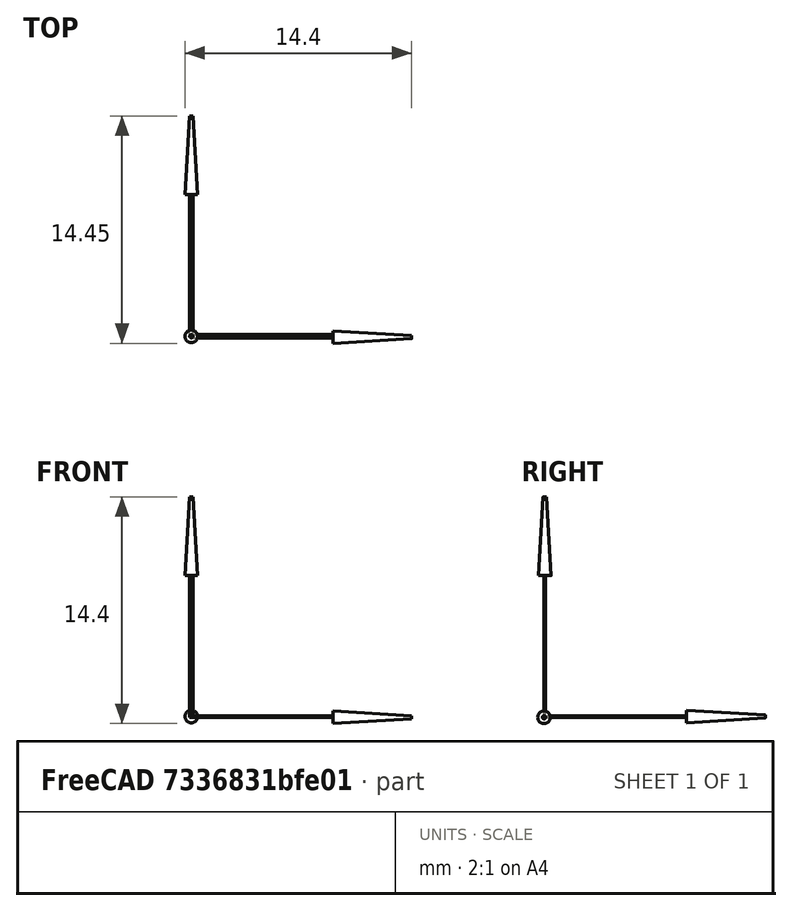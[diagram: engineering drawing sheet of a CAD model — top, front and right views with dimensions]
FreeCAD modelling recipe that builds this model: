
FCSTD DOCUMENT  (FreeCAD 0.16R6458 (Git))
Label: SSM-104-X-DH
License: All rights reserved
LicenseURL: http://en.wikipedia.org/wiki/All_rights_reserved
objects: Part::Feature×3, Sketcher::SketchObject×2, App::DocumentObjectGroup×1
note: 5 computed .brp shape members not serialized (recipe doc carries the construction recipe); baked Part::Feature solids carry a one-line shape summary decoded from their .brp

FEATURE [Part::Feature] FusionAxisZ1  label="Z"
  shape: bbox 0.8 x 0.8 x 14 mm, 8 faces (baked)
FEATURE [Part::Feature] FusionAxisY1  label="Y"
  Placement = pos=(0,0,0.05) rot=(-1,0,0;1.5708rad)
  shape: bbox 0.8 x 14 x 0.8 mm, 8 faces (baked)
FEATURE [Part::Feature] FusionAxisX1  label="X"
  Placement = pos=(0,-0.05,0) rot=(0,1,0;1.5708rad)
  shape: bbox 14 x 0.8 x 0.8 mm, 8 faces (baked)
FEATURE [App::DocumentObjectGroup] axis
  Group = -> [FusionAxisZ1,FusionAxisY1,FusionAxisX1]
FEATURE [Sketcher::SketchObject] Sketch  label="Footprint_Helper"
  expr: Constraints[124] = 4 * 2.54mm
  sketch-geometry (51):
    g0: LineSegment StartX=-11.98 StartY=4.32 StartZ=0 EndX=-9.695 EndY=4.32 EndZ=0
    g1: LineSegment StartX=-9.695 StartY=4.32 StartZ=0 EndX=-9.695 EndY=3.3 EndZ=0
    g2: LineSegment StartX=-9.695 StartY=3.3 StartZ=0 EndX=-11.98 EndY=3.3 EndZ=0
    g3: LineSegment StartX=-11.98 StartY=3.3 StartZ=0 EndX=-11.98 EndY=4.32 EndZ=0
    g4: LineSegment StartX=-11.98 StartY=1.78 StartZ=0 EndX=-9.695 EndY=1.78 EndZ=0
    g5: LineSegment StartX=-9.695 StartY=1.78 StartZ=0 EndX=-9.695 EndY=0.76 EndZ=0
    g6: LineSegment StartX=-9.695 StartY=0.76 StartZ=0 EndX=-11.98 EndY=0.76 EndZ=0
    g7: LineSegment StartX=-11.98 StartY=0.76 StartZ=0 EndX=-11.98 EndY=1.78 EndZ=0
    g8: LineSegment StartX=-11.98 StartY=-0.76 StartZ=0 EndX=-9.695 EndY=-0.76 EndZ=0
    g9: LineSegment StartX=-9.695 StartY=-0.76 StartZ=0 EndX=-9.695 EndY=-1.78 EndZ=0
    g10: LineSegment StartX=-9.695 StartY=-1.78 StartZ=0 EndX=-11.98 EndY=-1.78 EndZ=0
    g11: LineSegment StartX=-11.98 StartY=-1.78 StartZ=0 EndX=-11.98 EndY=-0.76 EndZ=0
    g12: LineSegment StartX=-11.98 StartY=-3.3 StartZ=0 EndX=-9.695 EndY=-3.3 EndZ=0
    g13: LineSegment StartX=-9.695 StartY=-3.3 StartZ=0 EndX=-9.695 EndY=-4.32 EndZ=0
    g14: LineSegment StartX=-9.695 StartY=-4.32 StartZ=0 EndX=-11.98 EndY=-4.32 EndZ=0
    g15: LineSegment StartX=-11.98 StartY=-4.32 StartZ=0 EndX=-11.98 EndY=-3.3 EndZ=0
    g16: LineSegment StartX=-2.585 StartY=-3.3 StartZ=0 EndX=-0.3 EndY=-3.3 EndZ=0
    g17: LineSegment StartX=-0.3 StartY=-3.3 StartZ=0 EndX=-0.3 EndY=-4.32 EndZ=0
    g18: LineSegment StartX=-0.3 StartY=-4.32 StartZ=0 EndX=-2.585 EndY=-4.32 EndZ=0
    g19: LineSegment StartX=-2.585 StartY=-4.32 StartZ=0 EndX=-2.585 EndY=-3.3 EndZ=0
    g20: LineSegment StartX=-2.585 StartY=-0.76 StartZ=0 EndX=-0.3 EndY=-0.76 EndZ=0
    g21: LineSegment StartX=-0.3 StartY=-0.76 StartZ=0 EndX=-0.3 EndY=-1.78 EndZ=0
    g22: LineSegment StartX=-0.3 StartY=-1.78 StartZ=0 EndX=-2.585 EndY=-1.78 EndZ=0
    g23: LineSegment StartX=-2.585 StartY=-1.78 StartZ=0 EndX=-2.585 EndY=-0.76 EndZ=0
    g24: LineSegment StartX=-2.585 StartY=1.78 StartZ=0 EndX=-0.3 EndY=1.78 EndZ=0
    g25: LineSegment StartX=-0.3 StartY=1.78 StartZ=0 EndX=-0.3 EndY=0.76 EndZ=0
    g26: LineSegment StartX=-0.3 StartY=0.76 StartZ=0 EndX=-2.585 EndY=0.76 EndZ=0
    g27: LineSegment StartX=-2.585 StartY=0.76 StartZ=0 EndX=-2.585 EndY=1.78 EndZ=0
    g28: LineSegment StartX=-2.585 StartY=4.32 StartZ=0 EndX=-0.3 EndY=4.32 EndZ=0
    g29: LineSegment StartX=-0.3 StartY=4.32 StartZ=0 EndX=-0.3 EndY=3.3 EndZ=0
    g30: LineSegment StartX=-0.3 StartY=3.3 StartZ=0 EndX=-2.585 EndY=3.3 EndZ=0
    g31: LineSegment StartX=-2.585 StartY=3.3 StartZ=0 EndX=-2.585 EndY=4.32 EndZ=0
    g32: LineSegment [constr] StartX=-10.8375 StartY=3.81 StartZ=0 EndX=-10.8375 EndY=1.27 EndZ=0
    g33: LineSegment [constr] StartX=-10.8375 StartY=1.27 StartZ=0 EndX=-10.8375 EndY=-1.27 EndZ=0
    g34: LineSegment [constr] StartX=-10.8375 StartY=-1.27 StartZ=0 EndX=-10.8375 EndY=-3.81 EndZ=0
    g35: LineSegment [constr] StartX=-1.4425 StartY=3.81 StartZ=0 EndX=-1.4425 EndY=1.27 EndZ=0
    g36: LineSegment [constr] StartX=-1.4425 StartY=1.27 StartZ=0 EndX=-1.4425 EndY=-1.27 EndZ=0
    g37: LineSegment [constr] StartX=-1.4425 StartY=-1.27 StartZ=0 EndX=-1.4425 EndY=-3.81 EndZ=0
    g38: LineSegment [constr] StartX=0 StartY=0 StartZ=0 EndX=-1.4425 EndY=0 EndZ=0
    g39: LineSegment [constr] StartX=-1.4425 StartY=0 StartZ=0 EndX=-10.8375 EndY=0 EndZ=0
    g40: LineSegment StartX=-10.205 StartY=5.08 StartZ=0 EndX=-2.075 EndY=5.08 EndZ=0
    g41: LineSegment StartX=-2.075 StartY=5.08 StartZ=0 EndX=-2.075 EndY=-5.08 EndZ=0
    g42: LineSegment StartX=-2.075 StartY=-5.08 StartZ=0 EndX=-10.205 EndY=-5.08 EndZ=0
    g43: LineSegment StartX=-10.205 StartY=-5.08 StartZ=0 EndX=-10.205 EndY=5.08 EndZ=0
    g44: LineSegment [constr] StartX=-2.075 StartY=0 StartZ=0 EndX=0 EndY=0 EndZ=0
    g45: LineSegment [constr] StartX=-2.075 StartY=5.08 StartZ=0 EndX=-0.3 EndY=5.08 EndZ=0
    g46: LineSegment [constr] StartX=-11.98 StartY=5.08 StartZ=0 EndX=-10.205 EndY=5.08 EndZ=0
    g47: LineSegment StartX=-12.25 StartY=5.35 StartZ=0 EndX=-0.05 EndY=5.35 EndZ=0
    g48: LineSegment StartX=-0.05 StartY=5.35 StartZ=0 EndX=-0.05 EndY=-5.35 EndZ=0
    g49: LineSegment StartX=-0.05 StartY=-5.35 StartZ=0 EndX=-12.25 EndY=-5.35 EndZ=0
    g50: LineSegment StartX=-12.25 StartY=-5.35 StartZ=0 EndX=-12.25 EndY=5.35 EndZ=0
  constraints (155):
    c: Coincident(g0,g1)
    c: Coincident(g1,g2)
    c: Coincident(g2,g3)
    c: Coincident(g3,g0)
    c: Horizontal(g0)
    c: Horizontal(g2)
    c: Vertical(g1)
    c: Vertical(g3)
    c: Coincident(g4,g5)
    c: Coincident(g5,g6)
    c: Coincident(g6,g7)
    c: Coincident(g7,g4)
    c: Horizontal(g4)
    c: Horizontal(g6)
    c: Vertical(g5)
    c: Vertical(g7)
    c: Coincident(g8,g9)
    c: Coincident(g9,g10)
    c: Coincident(g10,g11)
    c: Coincident(g11,g8)
    c: Horizontal(g8)
    c: Horizontal(g10)
    c: Vertical(g9)
    c: Vertical(g11)
    c: Coincident(g12,g13)
    c: Coincident(g13,g14)
    c: Coincident(g14,g15)
    c: Coincident(g15,g12)
    c: Horizontal(g12)
    c: Horizontal(g14)
    c: Vertical(g13)
    c: Vertical(g15)
    c: Coincident(g16,g17)
    c: Coincident(g17,g18)
    c: Coincident(g18,g19)
    c: Coincident(g19,g16)
    c: Horizontal(g16)
    c: Horizontal(g18)
    c: Vertical(g17)
    c: Vertical(g19)
    c: Coincident(g20,g21)
    c: Coincident(g21,g22)
    c: Coincident(g22,g23)
    c: Coincident(g23,g20)
    c: Horizontal(g20)
    c: Horizontal(g22)
    c: Vertical(g21)
    c: Vertical(g23)
    c: Coincident(g24,g25)
    c: Coincident(g25,g26)
    c: Coincident(g26,g27)
    c: Coincident(g27,g24)
    c: Horizontal(g24)
    c: Horizontal(g26)
    c: Vertical(g25)
    c: Vertical(g27)
    c: Coincident(g28,g29)
    c: Coincident(g29,g30)
    c: Coincident(g30,g31)
    c: Coincident(g31,g28)
    c: Horizontal(g28)
    c: Horizontal(g30)
    c: Vertical(g29)
    c: Vertical(g31)
    c: Equal(g8,g4)
    c: Equal(g4,g0)
    c: Equal(g0,g12)
    c: Equal(g28,g0)
    c: Equal(g28,g24)
    c: Equal(g24,g20)
    c: Equal(g20,g16)
    c: Equal(g19,g23)
    c: Equal(g23,g27)
    c: Equal(g27,g31)
    c: Equal(g3,g7)
    c: Equal(g7,g11)
    c: Equal(g11,g15)
    c: Equal(g3,g31)
    c: DistanceY(g3) = 1.02
    c: DistanceX(g0,g28) = 7.11
    c: DistanceX(g0,g28) = 11.68
    c: Vertical(g32)
    c: Coincident(g32,g33)
    c: Vertical(g33)
    c: Coincident(g33,g34)
    c: Coincident(g35,g36)
    c: Coincident(g36,g37)
    c: Vertical(g36)
    c: Vertical(g35)
    c: Vertical(g37)
    c: Vertical(g34)
    c: Equal(g32,g34)
    c: Equal(g34,g33)
    c: Equal(g36,g37)
    c: Equal(g37,g35)
    c: Equal(g32,g35)
    c: DistanceY(g32) = -2.54
    c: Symmetric(g14,g12,g34)
    c: Symmetric(g10,g8,g33)
    c: Symmetric(g6,g4,g32)
    c: Symmetric(g2,g0,g32)
    c: Symmetric(g26,g24,g35)
    c: Symmetric(g30,g28,g35)
    c: Symmetric(g20,g22,g36)
    c: Symmetric(g16,g18,g37)
    c: Horizontal(g38)
    c: Coincident(g38,g39)
    c: Horizontal(g39)
    c: Symmetric(g33,g33,g39)
    c: Symmetric(g36,g36,g38)
    c: Coincident(g-1,g38)
    c: Coincident(g40,g41)
    c: Coincident(g41,g42)
    c: Coincident(g42,g43)
    c: Coincident(g43,g40)
    c: Horizontal(g40)
    c: Horizontal(g42)
    c: Vertical(g41)
    c: Vertical(g43)
    c: DistanceX(g40) = 8.13
    c: Horizontal(g44)
    c: Symmetric(g41,g41,g44)
    c: DistanceX(g44) = 2.075
    c: Coincident(g44,g-1)
    c: DistanceY(g43) = 10.16
    c: Horizontal(g45)
    c: Horizontal(g46)
    c: Coincident(g46,g40)
    c: Coincident(g40,g45)
    c: PointOnObject(g45,g29)
    c: PointOnObject(g46,g3)
    c: Equal(g45,g46)
    c: Coincident(g47,g48)
    c: Coincident(g48,g49)
    c: Coincident(g49,g50)
    c: Coincident(g50,g47)
    c: Horizontal(g47)
    c: Horizontal(g49)
    c: Vertical(g48)
    c: Vertical(g50)
    c: DistanceX(g47,g28) = -0.25
    c: DistanceY(g45,g47) = 0.27
    c: DistanceX(g49) = -12.25
    c: DistanceY(g49) = -5.35
    c: DistanceX(g47,g0) = 0.27
    c: DistanceY(g42,g49) = -0.27
    c: DistanceY(g-1,g47) = 5.35
    c: DistanceX(g0) = 2.285
    c: DistanceX(g-1,g33) = -10.8375
    c: DistanceY(g-1,g45) = 5.08
    c: DistanceX(g-1,g25) = -0.3  'minmal distance to board edge'
    c: DistanceX(g-1,g40) = -10.205
    c: DistanceX(g-1,g37) = -1.4425
    c: DistanceY(g-1,g37) = -3.81
    c: DistanceY(g-1,g36) = -1.27
FEATURE [Sketcher::SketchObject] Sketch003  label="insertion_depth"
  sketch-geometry (6):
    g0: LineSegment StartX=0 StartY=7.5 StartZ=0 EndX=-8.13 EndY=7.5 EndZ=0
    g1: LineSegment StartX=-8.13 StartY=7.5 StartZ=0 EndX=-8.13 EndY=-7.5 EndZ=0
    g2: LineSegment StartX=-8.13 StartY=-7.5 StartZ=0 EndX=0 EndY=-7.5 EndZ=0
    g3: LineSegment StartX=0 StartY=-7.5 StartZ=0 EndX=0 EndY=7.5 EndZ=0
    g4: LineSegment StartX=-3.79 StartY=7.5 StartZ=0 EndX=-3.79 EndY=-7.5 EndZ=0
    g5: LineSegment StartX=-1.78 StartY=7.5 StartZ=0 EndX=-1.78 EndY=-7.5 EndZ=0
  constraints (20):
    c: Coincident(g0,g1)
    c: Coincident(g1,g2)
    c: Coincident(g2,g3)
    c: Coincident(g3,g0)
    c: Horizontal(g0)
    c: Horizontal(g2)
    c: Vertical(g1)
    c: Vertical(g3)
    c: DistanceY(g1) = -15
    c: Symmetric(g3,g3,g-1)
    c: DistanceX(g0) = -8.13
    c: Vertical(g4)
    c: PointOnObject(g4,g2)
    c: PointOnObject(g4,g0)
    c: DistanceX(g0,g4) = 4.34
    c: PointOnObject(g5,g0)
    c: PointOnObject(g5,g2)
    c: Vertical(g5)
    c: DistanceX(g5,g0) = -6.35
    c: DistanceX(g5,g0) = 1.78
